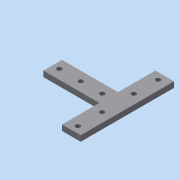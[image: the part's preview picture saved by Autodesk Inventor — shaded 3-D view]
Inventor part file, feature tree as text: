
AUTODESK INVENTOR PART (.ipt)
format: ipt  version: 2015 (Build 190159000, 159)  size: 100,352 bytes
history: native  units: mm
features: sketch x2, extrude x1, hole x1
ambient origin geometry x8: Origin, YZ Plane, XZ Plane, XY Plane, X Axis, Y Axis, Z Axis, Center Point
bodies: Solid1 (feature_tree)
feature tree (4):
  extrude  "Extrusion1"  Depth=100.0mm
  hole  "Hole1"  [1 undecoded]
  sketch  "Sketch1"  dims[d0=20.0mm d1=100.0mm]
  sketch  "Sketch2"  dims[d2=20.0mm d3=40.0mm d4=60.0mm d5=6.0mm d6=0.0mm d7=7.0mm d8=7.0mm d9=7.0mm d10=7.0mm d11=10.0mm d12=10.0mm d13=10.0mm d14=10.0mm d15=7.0mm d16=7.0mm d17=23.0mm d18=5.0mm d19=6.0mm d20=4.0mm d21=2.0mm d22=90.0deg d23=8.0mm d24=20.594885mm]
note: 1 required parameter value undecoded (feature->parameter linkage not recoverable at this tier; creation-order binding heuristic only, values carry confidence <= 0.55)
